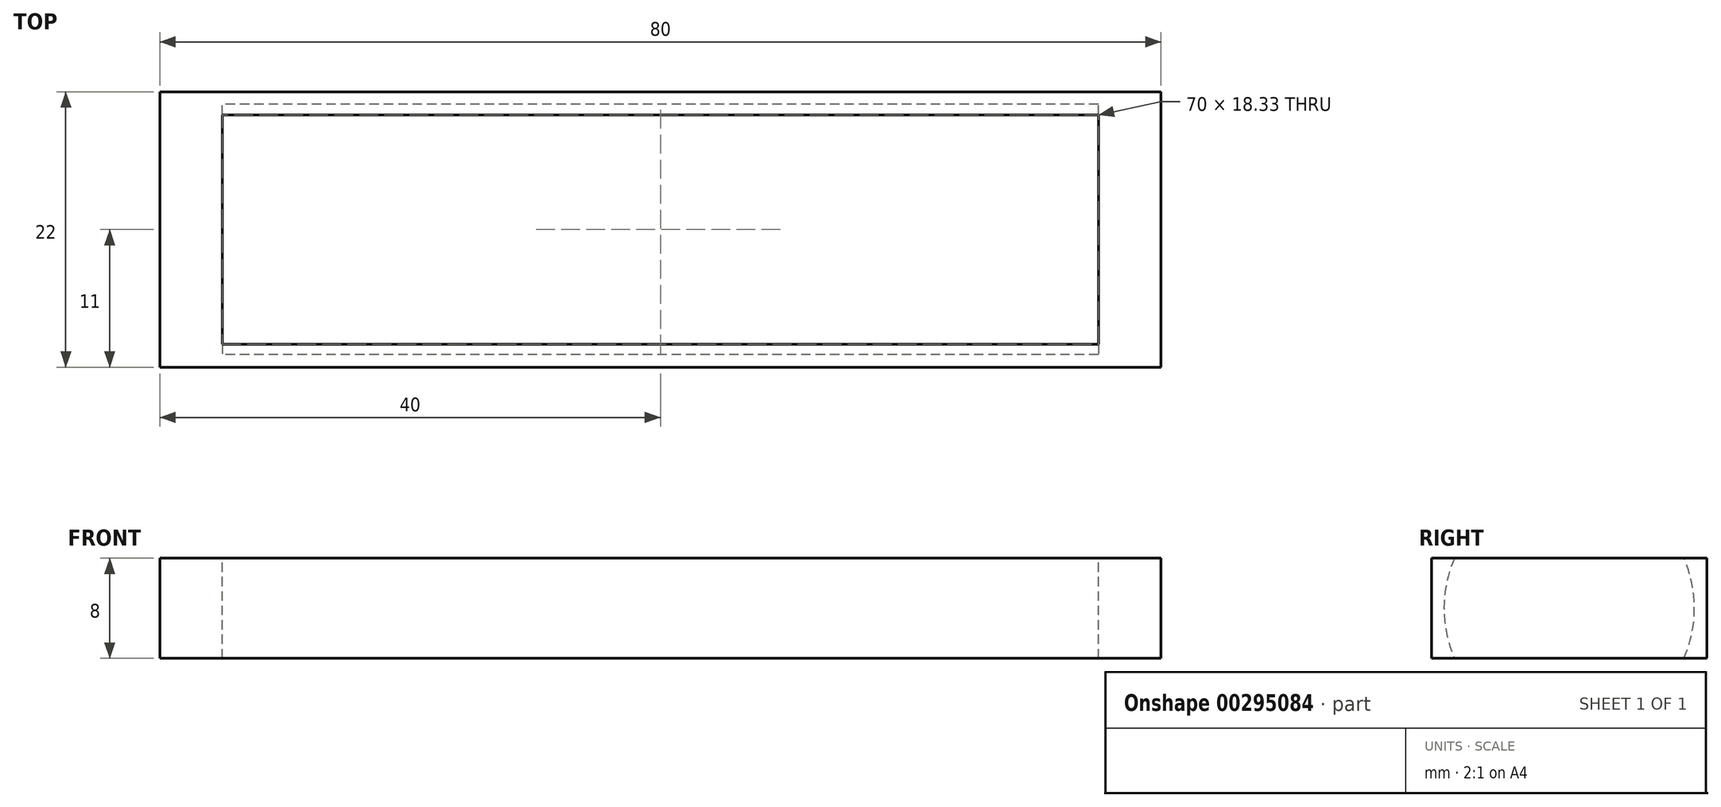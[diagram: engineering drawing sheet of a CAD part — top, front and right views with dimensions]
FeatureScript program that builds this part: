
annotation { "Feature Type Name" : "Feature", "Feature Type Description" : "" }
export const myFeature = defineFeature(function(context is Context, id is Id, definition is map)
    precondition{}
    {
        {
            var Q0;
            Q0=qCreatedBy(makeId("Right.planeOp"),FACE);
            var sketch = newSketch(context, id + "F0", { "sketchPlane" : qUnion([Q0])});
            skLineSegment(sketch, "E0.bottom", {"start": v(11, -4) * mm, "end": v(-11, -4) * mm});
            skLineSegment(sketch, "E0.top", {"start": v(11, 4) * mm, "end": v(-11, 4) * mm});
            skLineSegment(sketch, "E0.left", {"start": v(11, -4) * mm, "end": v(11, 4) * mm});
            skLineSegment(sketch, "E0.right", {"start": v(-11, -4) * mm, "end": v(-11, 4) * mm});
            skPoint(sketch, "E0.middle", {"position": v(0, 0) * mm});
            skArc(sketch, "E1", {"start": v(-9.17, 4) * mm, "mid": v(-10, 0) * mm, "end": v(-9.17, -4) * mm});
            skPoint(sketch, "E2", {"position": v(-9.17, -4) * mm});
            skPoint(sketch, "E3", {"position": v(-9.17, 4) * mm});
            skPoint(sketch, "E4", {"position": v(9.17, 4) * mm});
            skPoint(sketch, "E5", {"position": v(9.17, -4) * mm});
            skArc(sketch, "E6.trimOffspring", {"start": v(9.17, -4) * mm, "mid": v(10, 0) * mm, "end": v(9.17, 4) * mm});
            skSolve(sketch);
        }
        {
            var Q0;
            {var subQ0=sQuery(id+"F0.wireOp",EDGE,"E0.right");Q0=makeQuery(id+"F0.imprint","IMPRINT",FACE,{"disambiguationData":[TD([[makeQuery(id+"F0.imprint","IMPRINT",EDGE,{"derivedFrom":subQ0}),-1.0]])]});}
            var Q1;
            {var subQ0=sQuery(id+"F0.wireOp",EDGE,"E1");Q1=makeQuery(id+"F0.imprint","IMPRINT",FACE,{"disambiguationData":[TD([[makeQuery(id+"F0.imprint","IMPRINT",EDGE,{"derivedFrom":subQ0}),1.0]])]});}
            var Q2;
            {var subQ0=sQuery(id+"F0.wireOp",EDGE,"E0.left");Q2=makeQuery(id+"F0.imprint","IMPRINT",FACE,{"disambiguationData":[TD([[makeQuery(id+"F0.imprint","IMPRINT",EDGE,{"derivedFrom":subQ0}),1.0]])]});}
            extrude(context, id + "F1", {"entities" : qUnion([Q0, Q1, Q2]), "oppositeDirection" : true, "depth" : 5 * mm});
        }
        {
            var Q0;
            {var subQ0=sQuery(id+"F0.wireOp",EDGE,"E0.left");Q0=makeQuery(id+"F0.imprint","IMPRINT",FACE,{"disambiguationData":[TD([[makeQuery(id+"F0.imprint","IMPRINT",EDGE,{"derivedFrom":subQ0}),1.0]])]});}
            var Q1;
            {var subQ0=sQuery(id+"F0.wireOp",EDGE,"E1");Q1=makeQuery(id+"F0.imprint","IMPRINT",FACE,{"disambiguationData":[TD([[makeQuery(id+"F0.imprint","IMPRINT",EDGE,{"derivedFrom":subQ0}),1.0]])]});}
            var Q2;
            {var subQ0=sQuery(id+"F0.wireOp",EDGE,"E0.right");Q2=makeQuery(id+"F0.imprint","IMPRINT",FACE,{"disambiguationData":[TD([[makeQuery(id+"F0.imprint","IMPRINT",EDGE,{"derivedFrom":subQ0}),-1.0]])]});}
            extrude(context, id + "F2", {"entities" : qUnion([Q0, Q1, Q2]), "operationType" : NewBodyOperationType.ADD, "depth" : 75 * mm});
        }
        {
            var Q0;
            {var subQ0=sQuery(id+"F0.wireOp",EDGE,"E1");Q0=makeQuery(id+"F0.imprint","IMPRINT",FACE,{"disambiguationData":[TD([[makeQuery(id+"F0.imprint","IMPRINT",EDGE,{"derivedFrom":subQ0}),1.0]])]});}
            extrude(context, id + "F3", {"entities" : qUnion([Q0]), "operationType" : NewBodyOperationType.REMOVE, "depth" : 70 * mm});
        }
    });
